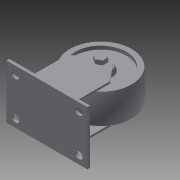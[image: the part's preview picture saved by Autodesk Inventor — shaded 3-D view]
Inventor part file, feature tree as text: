
AUTODESK INVENTOR PART (.ipt)
format: ipt  version: 2014 (Build 180170000, 170)  size: 210,944 bytes
history: native  units: in
note: dims shown in document units (in); Inventor stores cm internally (conversion verified against a paired STEP export)
features: imported_body x2, revolve x1, other x1, boolean_combine x1
ambient origin geometry x8: Origin, YZ Plane, XZ Plane, XY Plane, X Axis, Y Axis, Z Axis, Center Point
bodies: Body1 (feature_tree), Body2 (feature_tree)
feature tree (5):
  revolve  "Revolve1"  [1 undecoded]
  other  "2358T320_STATIC-CONTROL CASTER1"
  boolean_combine  "Combine1"
  imported_body  "Base1"
  imported_body  "Base2"
note: 1 required parameter value undecoded (feature->parameter linkage not recoverable at this tier; creation-order binding heuristic only, values carry confidence <= 0.55)
